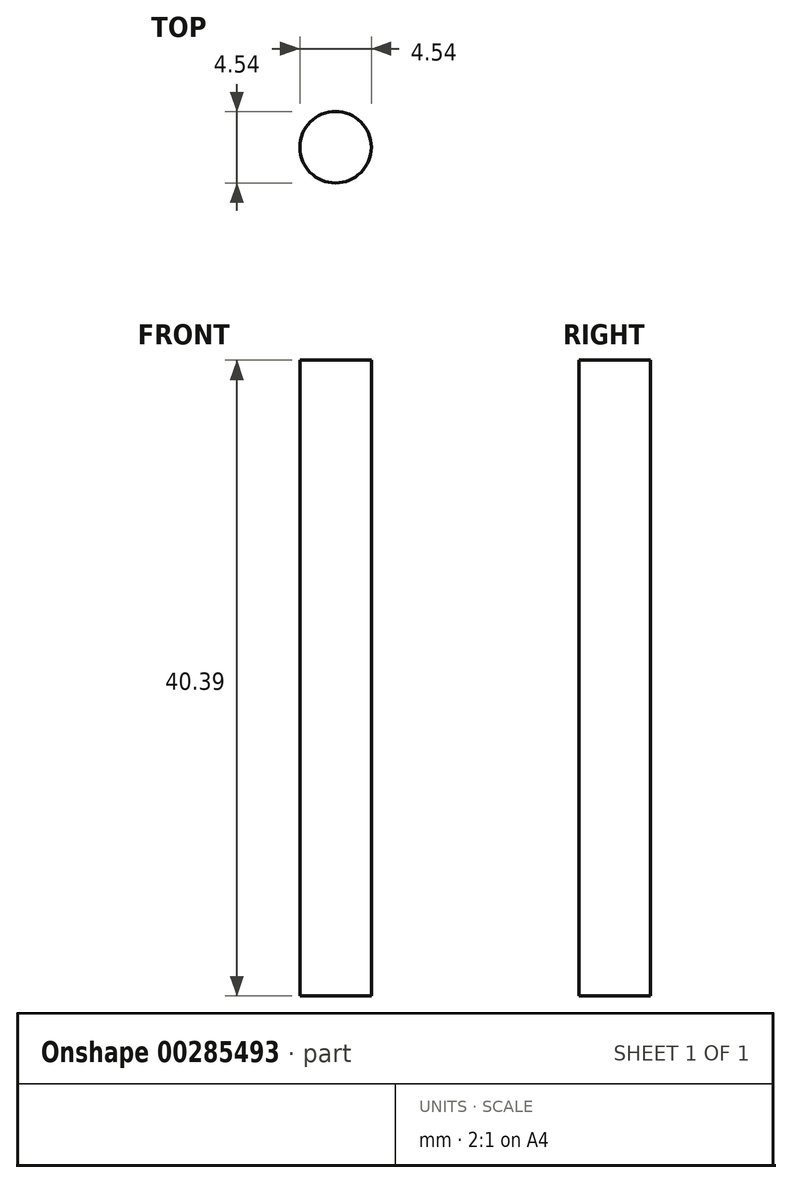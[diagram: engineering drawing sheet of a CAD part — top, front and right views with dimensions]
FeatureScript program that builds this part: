
annotation { "Feature Type Name" : "Feature", "Feature Type Description" : "" }
export const myFeature = defineFeature(function(context is Context, id is Id, definition is map)
    precondition{}
    {
        {
            var Q0;
            Q0=qCreatedBy(makeId("Top.planeOp"),FACE);
            var sketch = newSketch(context, id + "F0", { "sketchPlane" : qUnion([Q0])});
            skCircle(sketch, "E0", {"center": v(0, -35.12) * mm, "radius": 2.27 * mm});
            skSolve(sketch);
        }
        {
            var Q0;
            Q0=makeQuery(id+"F0.imprint","IMPRINT",FACE,{"disambiguationData":[TD([[makeQuery(id+"F0.imprint","IMPRINT",EDGE,{"derivedFrom":sQuery(id+"F0.wireOp",EDGE,"E0")}),1.0]])]});
            var Q1;
            Q1=sQuery(id+"F0.wireOp",EDGE,"E0");
            extrude(context, id + "F1", {"entities" : qUnion([Q0]), "surfaceEntities" : qUnion([Q1]), "depth" : 40.4 * mm});
        }
    });
